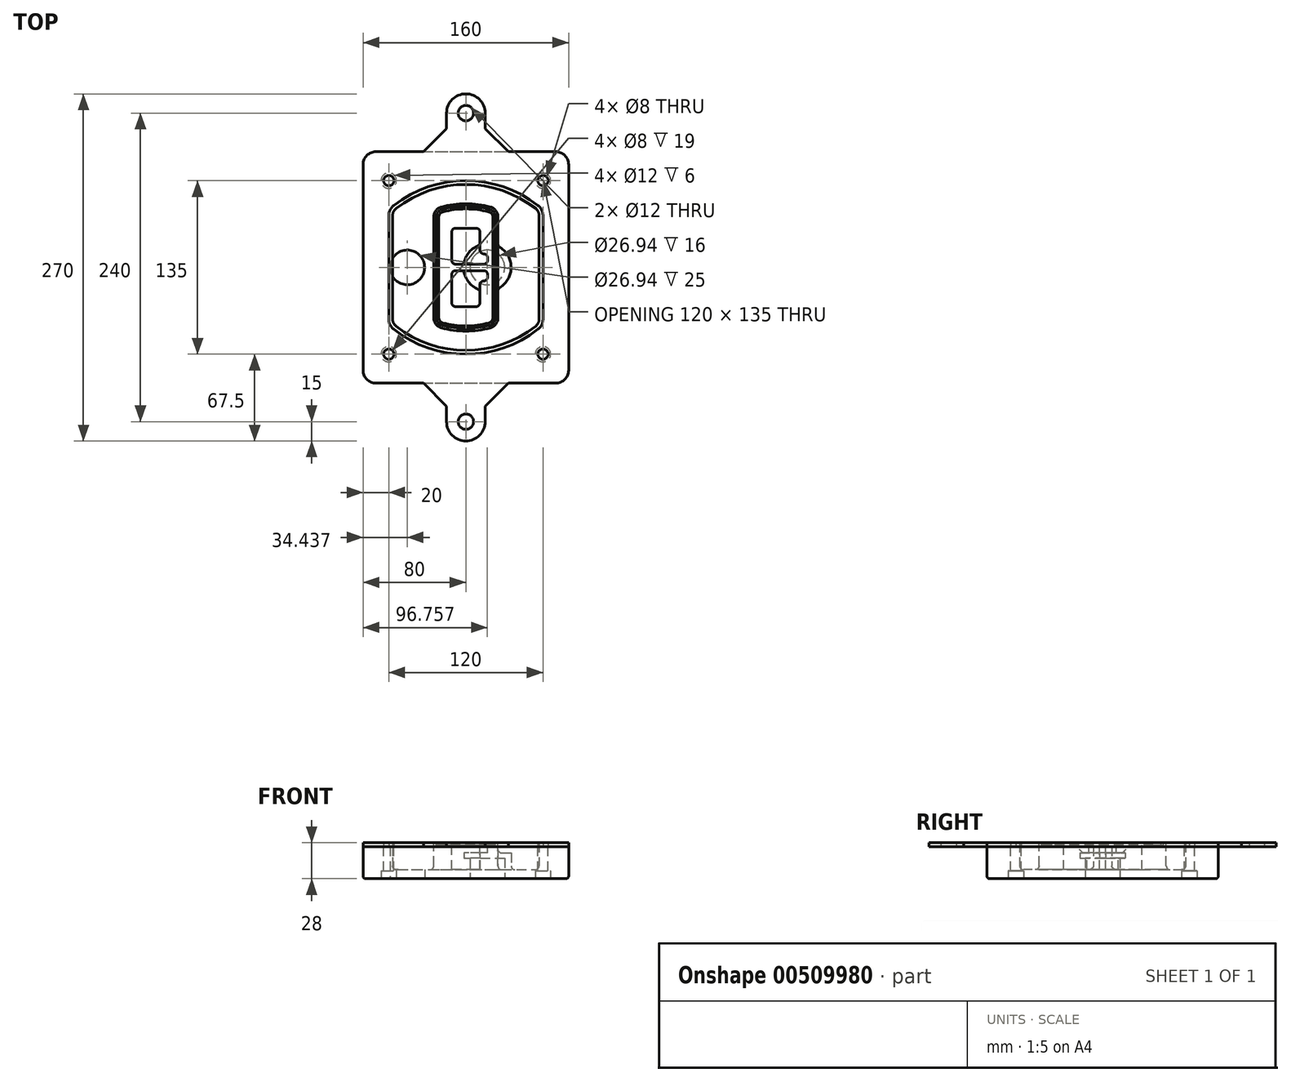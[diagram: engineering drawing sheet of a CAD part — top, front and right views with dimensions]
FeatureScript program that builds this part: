
annotation { "Feature Type Name" : "Feature", "Feature Type Description" : "" }
export const myFeature = defineFeature(function(context is Context, id is Id, definition is map)
    precondition{}
    {
        {
            var Q0;
            Q0=qCreatedBy(makeId("Top.planeOp"),FACE);
            var sketch = newSketch(context, id + "F0", { "sketchPlane" : qUnion([Q0])});
            skPoint(sketch, "E0.rect.middle", {"position": v(0, 0) * mm});
            skLineSegment(sketch, "E1.bottom", {"start": v(-70, -90) * mm, "end": v(70, -90) * mm});
            skLineSegment(sketch, "E1.top", {"start": v(-70, 90) * mm, "end": v(70, 90) * mm});
            skLineSegment(sketch, "E1.left", {"start": v(-80, -80) * mm, "end": v(-80, 80) * mm});
            skLineSegment(sketch, "E1.right", {"start": v(80, -80) * mm, "end": v(80, 80) * mm});
            skLineSegment(sketch, "E2", {"start": v(-80, 90) * mm, "end": v(80, -90) * mm, "construction": true});
            skLineSegment(sketch, "E3", {"start": v(80, 90) * mm, "end": v(-80, -90) * mm, "construction": true});
            skCircle(sketch, "E4", {"center": v(-60, 67.5) * mm, "radius": 4 * mm});
            skCircle(sketch, "E5", {"center": v(60, 67.5) * mm, "radius": 4 * mm});
            skCircle(sketch, "E6", {"center": v(60, -67.5) * mm, "radius": 4 * mm});
            skCircle(sketch, "E7", {"center": v(-60, -67.5) * mm, "radius": 4 * mm});
            skLineSegment(sketch, "E8", {"start": v(-60, 67.5) * mm, "end": v(60, 67.5) * mm, "construction": true});
            skLineSegment(sketch, "E9", {"start": v(60, 67.5) * mm, "end": v(60, -67.5) * mm, "construction": true});
            skLineSegment(sketch, "E10", {"start": v(60, -67.5) * mm, "end": v(-60, -67.5) * mm, "construction": true});
            skLineSegment(sketch, "E11", {"start": v(-60, -67.5) * mm, "end": v(-60, 67.5) * mm, "construction": true});
            skLineSegment(sketch, "E12", {"start": v(-60, 40.3) * mm, "end": v(-60, -40.3) * mm});
            skLineSegment(sketch, "E13", {"start": v(60, 40.3) * mm, "end": v(60, -40.3) * mm});
            skArc(sketch, "E14", {"start": v(56.15, 48.18) * mm, "mid": v(0, 67.5) * mm, "end": v(-56.15, 48.18) * mm});
            skArc(sketch, "E15", {"start": v(-56.15, -48.18) * mm, "mid": v(0, -67.5) * mm, "end": v(56.15, -48.18) * mm});
            skLineSegment(sketch, "E16", {"start": v(-60, 0) * mm, "end": v(60, 0) * mm, "construction": true});
            skPoint(sketch, "E17.visualSharp", {"position": v(-60, -45) * mm});
            skArc(sketch, "E17.filletArc", {"start": v(-60, -40.3) * mm, "mid": v(-58.99, -44.68) * mm, "end": v(-56.15, -48.18) * mm});
            skPoint(sketch, "E18.visualSharp", {"position": v(-60, 45) * mm});
            skArc(sketch, "E18.filletArc", {"start": v(-56.15, 48.18) * mm, "mid": v(-58.99, 44.68) * mm, "end": v(-60, 40.3) * mm});
            skPoint(sketch, "E19.visualSharp", {"position": v(60, 45) * mm});
            skArc(sketch, "E19.filletArc", {"start": v(60, 40.3) * mm, "mid": v(58.99, 44.68) * mm, "end": v(56.15, 48.18) * mm});
            skPoint(sketch, "E20.visualSharp", {"position": v(60, -45) * mm});
            skArc(sketch, "E20.filletArc", {"start": v(56.15, -48.18) * mm, "mid": v(58.99, -44.68) * mm, "end": v(60, -40.3) * mm});
            skPoint(sketch, "E21.visualSharp", {"position": v(-80, 90) * mm});
            skArc(sketch, "E21.filletArc", {"start": v(-70, 90) * mm, "mid": v(-77.07, 87.07) * mm, "end": v(-80, 80) * mm});
            skPoint(sketch, "E22.visualSharp", {"position": v(80, 90) * mm});
            skArc(sketch, "E22.filletArc", {"start": v(80, 80) * mm, "mid": v(77.07, 87.07) * mm, "end": v(70, 90) * mm});
            skPoint(sketch, "E23.visualSharp", {"position": v(80, -90) * mm});
            skArc(sketch, "E23.filletArc", {"start": v(70, -90) * mm, "mid": v(77.07, -87.07) * mm, "end": v(80, -80) * mm});
            skPoint(sketch, "E24.visualSharp", {"position": v(-80, -90) * mm});
            skArc(sketch, "E24.filletArc", {"start": v(-80, -80) * mm, "mid": v(-77.07, -87.07) * mm, "end": v(-70, -90) * mm});
            skArc(sketch, "E25.0", {"start": v(57, 40.3) * mm, "mid": v(56.3, 43.36) * mm, "end": v(54.3, 45.81) * mm});
            skLineSegment(sketch, "E25.1", {"start": v(57, 40.3) * mm, "end": v(57, -40.3) * mm});
            skArc(sketch, "E25.2", {"start": v(54.3, -45.81) * mm, "mid": v(56.3, -43.36) * mm, "end": v(57, -40.3) * mm});
            skArc(sketch, "E25.3", {"start": v(-54.3, -45.81) * mm, "mid": v(0, -64.5) * mm, "end": v(54.3, -45.81) * mm});
            skArc(sketch, "E25.4", {"start": v(-57, -40.3) * mm, "mid": v(-56.3, -43.36) * mm, "end": v(-54.3, -45.81) * mm});
            skArc(sketch, "E25.5", {"start": v(54.3, 45.81) * mm, "mid": v(0, 64.5) * mm, "end": v(-54.3, 45.81) * mm});
            skLineSegment(sketch, "E25.6", {"start": v(-57, 40.3) * mm, "end": v(-57, -40.3) * mm});
            skArc(sketch, "E25.7", {"start": v(-54.3, 45.81) * mm, "mid": v(-56.3, 43.36) * mm, "end": v(-57, 40.3) * mm});
            skArc(sketch, "E26.0", {"start": v(-58.62, 51.33) * mm, "mid": v(-62.58, 46.43) * mm, "end": v(-64, 40.3) * mm});
            skArc(sketch, "E26.1", {"start": v(58.62, 51.33) * mm, "mid": v(0, 71.5) * mm, "end": v(-58.62, 51.33) * mm});
            skArc(sketch, "E26.2", {"start": v(64, 40.3) * mm, "mid": v(62.58, 46.43) * mm, "end": v(58.62, 51.33) * mm});
            skLineSegment(sketch, "E26.3", {"start": v(64, 40.3) * mm, "end": v(64, -40.3) * mm});
            skArc(sketch, "E26.4", {"start": v(58.62, -51.33) * mm, "mid": v(62.58, -46.43) * mm, "end": v(64, -40.3) * mm});
            skLineSegment(sketch, "E26.5", {"start": v(-64, 40.3) * mm, "end": v(-64, -40.3) * mm});
            skArc(sketch, "E26.6", {"start": v(-58.62, -51.33) * mm, "mid": v(0, -71.5) * mm, "end": v(58.62, -51.33) * mm});
            skArc(sketch, "E26.7", {"start": v(-64, -40.3) * mm, "mid": v(-62.58, -46.43) * mm, "end": v(-58.62, -51.33) * mm});
            skSolve(sketch);
        }
        {
            var Q0;
            Q0=makeQuery(id+"F0.imprint","IMPRINT",FACE,{"disambiguationData":[TD([[makeQuery(id+"F0.imprint","IMPRINT",EDGE,{"derivedFrom":sQuery(id+"F0.wireOp",EDGE,"E1.bottom")}),1.0]])]});
            var Q1;
            Q1=makeQuery(id+"F0.imprint","IMPRINT",FACE,{"disambiguationData":[TD([[makeQuery(id+"F0.imprint","IMPRINT",EDGE,{"derivedFrom":sQuery(id+"F0.wireOp",EDGE,"E12")}),1.0]])]});
            var Q2;
            Q2=makeQuery(id+"F0.imprint","IMPRINT",FACE,{"disambiguationData":[TD([[makeQuery(id+"F0.imprint","IMPRINT",EDGE,{"derivedFrom":sQuery(id+"F0.wireOp",EDGE,"E25.0")}),1.0]])]});
            var Q3;
            Q3=makeQuery(id+"F0.imprint","IMPRINT",FACE,{"disambiguationData":[TD([[makeQuery(id+"F0.imprint","IMPRINT",EDGE,{"derivedFrom":sQuery(id+"F0.wireOp",EDGE,"E12")}),-1.0]])]});
            extrude(context, id + "F1", {"entities" : qUnion([Q0, Q1, Q2, Q3]), "oppositeDirection" : true, "depth" : 25 * mm});
        }
        {
            var Q0;
            Q0=makeQuery(id+"F0.imprint","IMPRINT",FACE,{"disambiguationData":[TD([[makeQuery(id+"F0.imprint","IMPRINT",EDGE,{"derivedFrom":sQuery(id+"F0.wireOp",EDGE,"E12")}),1.0]])]});
            extrude(context, id + "F2", {"entities" : qUnion([Q0]), "operationType" : NewBodyOperationType.ADD, "depth" : 3 * mm});
        }
        {
            var Q0;
            Q0=makeQuery(id+"F0.imprint","IMPRINT",FACE,{"disambiguationData":[TD([[makeQuery(id+"F0.imprint","IMPRINT",EDGE,{"derivedFrom":sQuery(id+"F0.wireOp",EDGE,"E25.0")}),1.0]])]});
            extrude(context, id + "F3", {"entities" : qUnion([Q0]), "operationType" : NewBodyOperationType.REMOVE, "oppositeDirection" : true, "depth" : 18 * mm});
        }
        {
            var Q0;
            Q0=makeQuery(id+"F2.opExtrude","CAP_FACE",FACE,{"disambiguationData":[OSD([sQuery(id+"F0.wireOp",EDGE,"E12"),sQuery(id+"F0.wireOp",EDGE,"E13"),sQuery(id+"F0.wireOp",EDGE,"E14"),sQuery(id+"F0.wireOp",EDGE,"E15"),sQuery(id+"F0.wireOp",EDGE,"E17.filletArc"),sQuery(id+"F0.wireOp",EDGE,"E18.filletArc"),sQuery(id+"F0.wireOp",EDGE,"E19.filletArc"),sQuery(id+"F0.wireOp",EDGE,"E20.filletArc"),sQuery(id+"F0.wireOp",EDGE,"E25.0"),sQuery(id+"F0.wireOp",EDGE,"E25.1"),sQuery(id+"F0.wireOp",EDGE,"E25.2"),sQuery(id+"F0.wireOp",EDGE,"E25.3"),sQuery(id+"F0.wireOp",EDGE,"E25.4"),sQuery(id+"F0.wireOp",EDGE,"E25.5"),sQuery(id+"F0.wireOp",EDGE,"E25.6"),sQuery(id+"F0.wireOp",EDGE,"E25.7")])],"isStart":false});
            var sketch = newSketch(context, id + "F4", { "sketchPlane" : qUnion([Q0])});
            skArc(sketch, "E27.0", {"start": v(-19.08, -46.97) * mm, "mid": v(0, -49.5) * mm, "end": v(19.08, -46.97) * mm});
            skArc(sketch, "E28.0", {"start": v(19.08, 46.97) * mm, "mid": v(0, 49.5) * mm, "end": v(-19.08, 46.97) * mm});
            skLineSegment(sketch, "E29", {"start": v(-25, 39.25) * mm, "end": v(-25, -39.25) * mm});
            skLineSegment(sketch, "E30", {"start": v(25, 39.25) * mm, "end": v(25, -39.25) * mm});
            skLineSegment(sketch, "E31", {"start": v(-25, 45.1) * mm, "end": v(25, 45.1) * mm, "construction": true});
            skLineSegment(sketch, "E32", {"start": v(-25, -45.1) * mm, "end": v(25, -45.1) * mm, "construction": true});
            skPoint(sketch, "E33.visualSharp", {"position": v(-25, 45.1) * mm});
            skArc(sketch, "E33.filletArc", {"start": v(-19.08, 46.97) * mm, "mid": v(-23.35, 44.11) * mm, "end": v(-25, 39.25) * mm});
            skPoint(sketch, "E34.visualSharp", {"position": v(25, 45.1) * mm});
            skArc(sketch, "E34.filletArc", {"start": v(25, 39.25) * mm, "mid": v(23.35, 44.11) * mm, "end": v(19.08, 46.97) * mm});
            skPoint(sketch, "E35.visualSharp", {"position": v(25, -45.1) * mm});
            skArc(sketch, "E35.filletArc", {"start": v(19.08, -46.97) * mm, "mid": v(23.35, -44.11) * mm, "end": v(25, -39.25) * mm});
            skPoint(sketch, "E36.visualSharp", {"position": v(-25, -45.1) * mm});
            skArc(sketch, "E36.filletArc", {"start": v(-25, -39.25) * mm, "mid": v(-23.35, -44.11) * mm, "end": v(-19.08, -46.97) * mm});
            skArc(sketch, "E37.0", {"start": v(54.3, 45.81) * mm, "mid": v(0, 64.5) * mm, "end": v(-54.3, 45.81) * mm});
            skArc(sketch, "E37.1", {"start": v(-54.3, 45.81) * mm, "mid": v(-56.3, 43.36) * mm, "end": v(-57, 40.3) * mm});
            skLineSegment(sketch, "E37.2", {"start": v(-57, 40.3) * mm, "end": v(-57, -40.3) * mm});
            skArc(sketch, "E37.3", {"start": v(-57, -40.3) * mm, "mid": v(-56.3, -43.36) * mm, "end": v(-54.3, -45.81) * mm});
            skArc(sketch, "E37.4", {"start": v(-54.3, -45.81) * mm, "mid": v(0, -64.5) * mm, "end": v(54.3, -45.81) * mm});
            skArc(sketch, "E37.5", {"start": v(54.3, -45.81) * mm, "mid": v(56.3, -43.36) * mm, "end": v(57, -40.3) * mm});
            skLineSegment(sketch, "E37.6", {"start": v(57, 40.3) * mm, "end": v(57, -40.3) * mm});
            skArc(sketch, "E37.7", {"start": v(57, 40.3) * mm, "mid": v(56.3, 43.36) * mm, "end": v(54.3, 45.81) * mm});
            skLineSegment(sketch, "E38.0", {"start": v(23, 39.25) * mm, "end": v(23, -39.25) * mm});
            skArc(sketch, "E38.1", {"start": v(18.56, -45.04) * mm, "mid": v(21.76, -42.9) * mm, "end": v(23, -39.25) * mm});
            skArc(sketch, "E38.2", {"start": v(-18.56, -45.04) * mm, "mid": v(0, -47.5) * mm, "end": v(18.56, -45.04) * mm});
            skArc(sketch, "E38.3", {"start": v(-23, -39.25) * mm, "mid": v(-21.76, -42.9) * mm, "end": v(-18.56, -45.04) * mm});
            skLineSegment(sketch, "E38.4", {"start": v(-23, 39.25) * mm, "end": v(-23, -39.25) * mm});
            skArc(sketch, "E38.5", {"start": v(23, 39.25) * mm, "mid": v(21.76, 42.9) * mm, "end": v(18.56, 45.04) * mm});
            skArc(sketch, "E38.6", {"start": v(-18.56, 45.04) * mm, "mid": v(-21.76, 42.9) * mm, "end": v(-23, 39.25) * mm});
            skArc(sketch, "E38.7", {"start": v(18.56, 45.04) * mm, "mid": v(0, 47.5) * mm, "end": v(-18.56, 45.04) * mm});
            skArc(sketch, "E39.0", {"start": v(21, 39.25) * mm, "mid": v(20.18, 41.68) * mm, "end": v(18.04, 43.1) * mm});
            skLineSegment(sketch, "E39.1", {"start": v(21, 39.25) * mm, "end": v(21, -39.25) * mm});
            skArc(sketch, "E39.2", {"start": v(18.04, -43.1) * mm, "mid": v(20.18, -41.68) * mm, "end": v(21, -39.25) * mm});
            skArc(sketch, "E39.3", {"start": v(-18.04, -43.1) * mm, "mid": v(0, -45.5) * mm, "end": v(18.04, -43.1) * mm});
            skArc(sketch, "E39.4", {"start": v(-21, -39.25) * mm, "mid": v(-20.18, -41.68) * mm, "end": v(-18.04, -43.1) * mm});
            skArc(sketch, "E39.5", {"start": v(18.04, 43.1) * mm, "mid": v(0, 45.5) * mm, "end": v(-18.04, 43.1) * mm});
            skLineSegment(sketch, "E39.6", {"start": v(-21, 39.25) * mm, "end": v(-21, -39.25) * mm});
            skArc(sketch, "E39.7", {"start": v(-18.04, 43.1) * mm, "mid": v(-20.18, 41.68) * mm, "end": v(-21, 39.25) * mm});
            skLineSegment(sketch, "E40", {"start": v(-25, 0) * mm, "end": v(25, 0) * mm, "construction": true});
            skLineSegment(sketch, "E41", {"start": v(-11, 5.5) * mm, "end": v(-11, 27.5) * mm});
            skLineSegment(sketch, "E42", {"start": v(-8, 30.5) * mm, "end": v(8, 30.5) * mm});
            skLineSegment(sketch, "E43", {"start": v(11, 27.5) * mm, "end": v(11, 13.5) * mm});
            skLineSegment(sketch, "E44", {"start": v(14, 10.5) * mm, "end": v(14, 10.5) * mm});
            skLineSegment(sketch, "E45", {"start": v(17, 7.5) * mm, "end": v(17, 5.5) * mm});
            skLineSegment(sketch, "E46", {"start": v(14, 2.5) * mm, "end": v(-8, 2.5) * mm});
            skPoint(sketch, "E47.visualSharp", {"position": v(-11, 30.5) * mm});
            skArc(sketch, "E47.filletArc", {"start": v(-8, 30.5) * mm, "mid": v(-10.12, 29.62) * mm, "end": v(-11, 27.5) * mm});
            skPoint(sketch, "E48.visualSharp", {"position": v(11, 30.5) * mm});
            skArc(sketch, "E48.filletArc", {"start": v(11, 27.5) * mm, "mid": v(10.12, 29.62) * mm, "end": v(8, 30.5) * mm});
            skPoint(sketch, "E49.visualSharp", {"position": v(11, 10.5) * mm});
            skArc(sketch, "E49.filletArc", {"start": v(11, 13.5) * mm, "mid": v(11.88, 11.38) * mm, "end": v(14, 10.5) * mm});
            skPoint(sketch, "E50.visualSharp", {"position": v(17, 10.5) * mm});
            skArc(sketch, "E50.filletArc", {"start": v(17, 7.5) * mm, "mid": v(16.12, 9.62) * mm, "end": v(14, 10.5) * mm});
            skPoint(sketch, "E51.visualSharp", {"position": v(17, 2.5) * mm});
            skArc(sketch, "E51.filletArc", {"start": v(14, 2.5) * mm, "mid": v(16.12, 3.38) * mm, "end": v(17, 5.5) * mm});
            skPoint(sketch, "E52.visualSharp", {"position": v(-11, 2.5) * mm});
            skArc(sketch, "E52.filletArc", {"start": v(-11, 5.5) * mm, "mid": v(-10.12, 3.38) * mm, "end": v(-8, 2.5) * mm});
            skLineSegment(sketch, "E53.0.MirrorCS", {"start": v(14, -2.5) * mm, "end": v(-8, -2.5) * mm});
            skArc(sketch, "E54.0.MirrorCS", {"start": v(-11, -5.5) * mm, "mid": v(-10.12, -3.38) * mm, "end": v(-8, -2.5) * mm});
            skLineSegment(sketch, "E55.0.MirrorCS", {"start": v(-11, -5.5) * mm, "end": v(-11, -27.5) * mm});
            skArc(sketch, "E56.0.MirrorCS", {"start": v(-8, -30.5) * mm, "mid": v(-10.12, -29.62) * mm, "end": v(-11, -27.5) * mm});
            skLineSegment(sketch, "E57.0.MirrorCS", {"start": v(-8, -30.5) * mm, "end": v(8, -30.5) * mm});
            skArc(sketch, "E58.0.MirrorCS", {"start": v(11, -27.5) * mm, "mid": v(10.12, -29.62) * mm, "end": v(8, -30.5) * mm});
            skLineSegment(sketch, "E59.0.MirrorCS", {"start": v(11, -27.5) * mm, "end": v(11, -13.5) * mm});
            skArc(sketch, "E60.0.MirrorCS", {"start": v(11, -13.5) * mm, "mid": v(11.88, -11.38) * mm, "end": v(14, -10.5) * mm});
            skArc(sketch, "E61.0.MirrorCS", {"start": v(17, -7.5) * mm, "mid": v(16.12, -9.62) * mm, "end": v(14, -10.5) * mm});
            skLineSegment(sketch, "E62.0.MirrorCS", {"start": v(17, -7.5) * mm, "end": v(17, -5.5) * mm});
            skArc(sketch, "E63.0.MirrorCS", {"start": v(14, -2.5) * mm, "mid": v(16.12, -3.38) * mm, "end": v(17, -5.5) * mm});
            skSolve(sketch);
        }
        {
            var Q0;
            Q0=makeQuery(id+"F4.imprint","IMPRINT",FACE,{"disambiguationData":[TD([[makeQuery(id+"F4.imprint","IMPRINT",EDGE,{"derivedFrom":sQuery(id+"F4.wireOp",EDGE,"E27.0")}),1.0]])]});
            var Q1;
            Q1=makeQuery(id+"F4.imprint","IMPRINT",FACE,{"disambiguationData":[TD([[makeQuery(id+"F4.imprint","IMPRINT",EDGE,{"derivedFrom":sQuery(id+"F4.wireOp",EDGE,"E38.0")}),-1.0]])]});
            var Q2;
            Q2=makeQuery(id+"F4.imprint","IMPRINT",FACE,{"disambiguationData":[TD([[makeQuery(id+"F4.imprint","IMPRINT",EDGE,{"derivedFrom":sQuery(id+"F4.wireOp",EDGE,"E39.0")}),1.0]])]});
            extrude(context, id + "F5", {"entities" : qUnion([Q0, Q1, Q2]), "operationType" : NewBodyOperationType.ADD, "endBound" : BoundingType.UP_TO_NEXT, "oppositeDirection" : true, "depth" : 25 * mm});
        }
        {
            var Q0;
            Q0=makeQuery(id+"F4.imprint","IMPRINT",FACE,{"disambiguationData":[TD([[makeQuery(id+"F4.imprint","IMPRINT",EDGE,{"derivedFrom":sQuery(id+"F4.wireOp",EDGE,"E38.0")}),-1.0]])]});
            extrude(context, id + "F6", {"entities" : qUnion([Q0]), "operationType" : NewBodyOperationType.REMOVE, "oppositeDirection" : true, "depth" : 2 * mm});
        }
        {
            var Q0;
            Q0=makeQuery(id+"F1.opExtrude","CAP_FACE",FACE,{"disambiguationData":[OSD([sQuery(id+"F0.wireOp",EDGE,"E1.bottom"),sQuery(id+"F0.wireOp",EDGE,"E1.top"),sQuery(id+"F0.wireOp",EDGE,"E1.left"),sQuery(id+"F0.wireOp",EDGE,"E1.right"),sQuery(id+"F0.wireOp",EDGE,"E4"),sQuery(id+"F0.wireOp",EDGE,"E5"),sQuery(id+"F0.wireOp",EDGE,"E6"),sQuery(id+"F0.wireOp",EDGE,"E7"),sQuery(id+"F0.wireOp",EDGE,"E21.filletArc"),sQuery(id+"F0.wireOp",EDGE,"E22.filletArc"),sQuery(id+"F0.wireOp",EDGE,"E23.filletArc"),sQuery(id+"F0.wireOp",EDGE,"E24.filletArc")])],"isStart":false});
            var sketch = newSketch(context, id + "F7", { "sketchPlane" : qUnion([Q0])});
            skCircle(sketch, "E64", {"center": v(16.76, 0) * mm, "radius": 13.47 * mm});
            skCircle(sketch, "E65", {"center": v(-45.56, 0) * mm, "radius": 13.47 * mm});
            skLineSegment(sketch, "E66", {"start": v(80, 0) * mm, "end": v(-80, 0) * mm});
            skCircle(sketch, "E67", {"center": v(16.76, 0) * mm, "radius": 18.47 * mm});
            skCircle(sketch, "E68", {"center": v(60, -67.5) * mm, "radius": 6 * mm});
            skCircle(sketch, "E69", {"center": v(-60, -67.5) * mm, "radius": 6 * mm});
            skCircle(sketch, "E70", {"center": v(-60, 67.5) * mm, "radius": 6 * mm});
            skCircle(sketch, "E71", {"center": v(60, 67.5) * mm, "radius": 6 * mm});
            skSolve(sketch);
        }
        {
            var Q0;
            {var subQ1=sQuery(id+"F7.wireOp",EDGE,"E66");var subQ4=sQuery(id+"F7.wireOp",EDGE,"E64");var subQ6=makeQuery(id+"F7.imprint","INTERSECT",VERTEX,{"disambiguationData":[OD(0.0)],"derivedFrom":[subQ4,subQ1]});Q0=makeQuery(id+"F7.imprint","IMPRINT",FACE,{"disambiguationData":[TD([[makeQuery(id+"F7.imprint","IMPRINT",EDGE,{"disambiguationData":[TD([[subQ6,-1.0]])],"derivedFrom":subQ4}),-1.0]])]});}
            var Q1;
            {var subQ0=sQuery(id+"F7.wireOp",EDGE,"E66");var subQ1=sQuery(id+"F7.wireOp",EDGE,"E64");var subQ3=makeQuery(id+"F7.imprint","INTERSECT",VERTEX,{"disambiguationData":[OD(0.0)],"derivedFrom":[subQ1,subQ0]});Q1=makeQuery(id+"F7.imprint","IMPRINT",FACE,{"disambiguationData":[TD([[makeQuery(id+"F7.imprint","IMPRINT",EDGE,{"disambiguationData":[TD([[subQ3,-1.0]])],"derivedFrom":subQ1}),1.0]])]});}
            var Q2;
            {var subQ0=sQuery(id+"F7.wireOp",EDGE,"E66");var subQ1=sQuery(id+"F7.wireOp",EDGE,"E64");var subQ3=makeQuery(id+"F7.imprint","INTERSECT",VERTEX,{"disambiguationData":[OD(0.0)],"derivedFrom":[subQ1,subQ0]});Q2=makeQuery(id+"F7.imprint","IMPRINT",FACE,{"disambiguationData":[TD([[makeQuery(id+"F7.imprint","IMPRINT",EDGE,{"disambiguationData":[TD([[subQ3,1.0]])],"derivedFrom":subQ1}),1.0]])]});}
            var Q3;
            {var subQ1=sQuery(id+"F7.wireOp",EDGE,"E66");var subQ4=sQuery(id+"F7.wireOp",EDGE,"E64");var subQ6=makeQuery(id+"F7.imprint","INTERSECT",VERTEX,{"disambiguationData":[OD(0.0)],"derivedFrom":[subQ4,subQ1]});Q3=makeQuery(id+"F7.imprint","IMPRINT",FACE,{"disambiguationData":[TD([[makeQuery(id+"F7.imprint","IMPRINT",EDGE,{"disambiguationData":[TD([[subQ6,1.0]])],"derivedFrom":subQ4}),-1.0]])]});}
            extrude(context, id + "F8", {"entities" : qUnion([Q0, Q1, Q2, Q3]), "operationType" : NewBodyOperationType.ADD, "oppositeDirection" : true, "depth" : 20 * mm});
        }
        {
            var Q0;
            {var subQ0=sQuery(id+"F7.wireOp",EDGE,"E66");var subQ1=sQuery(id+"F7.wireOp",EDGE,"E64");var subQ3=makeQuery(id+"F7.imprint","INTERSECT",VERTEX,{"disambiguationData":[OD(0.0)],"derivedFrom":[subQ1,subQ0]});Q0=makeQuery(id+"F7.imprint","IMPRINT",FACE,{"disambiguationData":[TD([[makeQuery(id+"F7.imprint","IMPRINT",EDGE,{"disambiguationData":[TD([[subQ3,-1.0]])],"derivedFrom":subQ1}),1.0]])]});}
            var Q1;
            {var subQ0=sQuery(id+"F7.wireOp",EDGE,"E66");var subQ1=sQuery(id+"F7.wireOp",EDGE,"E64");var subQ3=makeQuery(id+"F7.imprint","INTERSECT",VERTEX,{"disambiguationData":[OD(0.0)],"derivedFrom":[subQ1,subQ0]});Q1=makeQuery(id+"F7.imprint","IMPRINT",FACE,{"disambiguationData":[TD([[makeQuery(id+"F7.imprint","IMPRINT",EDGE,{"disambiguationData":[TD([[subQ3,1.0]])],"derivedFrom":subQ1}),1.0]])]});}
            extrude(context, id + "F9", {"entities" : qUnion([Q0, Q1]), "operationType" : NewBodyOperationType.REMOVE, "oppositeDirection" : true, "depth" : 16 * mm});
        }
        {
            var Q0;
            {var subQ0=sQuery(id+"F7.wireOp",EDGE,"E66");var subQ1=sQuery(id+"F7.wireOp",EDGE,"E65");var subQ3=makeQuery(id+"F7.imprint","INTERSECT",VERTEX,{"disambiguationData":[OD(0.0)],"derivedFrom":[subQ1,subQ0]});Q0=makeQuery(id+"F7.imprint","IMPRINT",FACE,{"disambiguationData":[TD([[makeQuery(id+"F7.imprint","IMPRINT",EDGE,{"disambiguationData":[TD([[subQ3,-1.0]])],"derivedFrom":subQ1}),1.0]])]});}
            var Q1;
            {var subQ0=sQuery(id+"F7.wireOp",EDGE,"E66");var subQ1=sQuery(id+"F7.wireOp",EDGE,"E65");var subQ3=makeQuery(id+"F7.imprint","INTERSECT",VERTEX,{"disambiguationData":[OD(0.0)],"derivedFrom":[subQ1,subQ0]});Q1=makeQuery(id+"F7.imprint","IMPRINT",FACE,{"disambiguationData":[TD([[makeQuery(id+"F7.imprint","IMPRINT",EDGE,{"disambiguationData":[TD([[subQ3,1.0]])],"derivedFrom":subQ1}),1.0]])]});}
            extrude(context, id + "F10", {"entities" : qUnion([Q0, Q1]), "operationType" : NewBodyOperationType.REMOVE, "oppositeDirection" : true, "depth" : 25 * mm});
        }
        {
            var Q0;
            Q0=makeQuery(id+"F7.imprint","IMPRINT",FACE,{"disambiguationData":[TD([[makeQuery(id+"F7.imprint","IMPRINT",EDGE,{"derivedFrom":sQuery(id+"F7.wireOp",EDGE,"E68")}),1.0]])]});
            var Q1;
            Q1=makeQuery(id+"F7.imprint","IMPRINT",FACE,{"disambiguationData":[TD([[makeQuery(id+"F7.imprint","IMPRINT",EDGE,{"derivedFrom":makeQuery(id+"F1.opExtrude","CAP_EDGE",EDGE,{"disambiguationData":[OSD([sQuery(id+"F0.wireOp",EDGE,"E5")])],"isStart":false})}),-1.0]])]});
            var Q2;
            Q2=makeQuery(id+"F7.imprint","IMPRINT",FACE,{"disambiguationData":[TD([[makeQuery(id+"F7.imprint","IMPRINT",EDGE,{"derivedFrom":sQuery(id+"F7.wireOp",EDGE,"E69")}),1.0]])]});
            var Q3;
            Q3=makeQuery(id+"F7.imprint","IMPRINT",FACE,{"disambiguationData":[TD([[makeQuery(id+"F7.imprint","IMPRINT",EDGE,{"derivedFrom":makeQuery(id+"F1.opExtrude","CAP_EDGE",EDGE,{"disambiguationData":[OSD([sQuery(id+"F0.wireOp",EDGE,"E4")])],"isStart":false})}),-1.0]])]});
            var Q4;
            Q4=makeQuery(id+"F7.imprint","IMPRINT",FACE,{"disambiguationData":[TD([[makeQuery(id+"F7.imprint","IMPRINT",EDGE,{"derivedFrom":sQuery(id+"F7.wireOp",EDGE,"E70")}),1.0]])]});
            var Q5;
            Q5=makeQuery(id+"F7.imprint","IMPRINT",FACE,{"disambiguationData":[TD([[makeQuery(id+"F7.imprint","IMPRINT",EDGE,{"derivedFrom":makeQuery(id+"F1.opExtrude","CAP_EDGE",EDGE,{"disambiguationData":[OSD([sQuery(id+"F0.wireOp",EDGE,"E7")])],"isStart":false})}),-1.0]])]});
            var Q6;
            Q6=makeQuery(id+"F7.imprint","IMPRINT",FACE,{"disambiguationData":[TD([[makeQuery(id+"F7.imprint","IMPRINT",EDGE,{"derivedFrom":sQuery(id+"F7.wireOp",EDGE,"E71")}),1.0]])]});
            var Q7;
            Q7=makeQuery(id+"F7.imprint","IMPRINT",FACE,{"disambiguationData":[TD([[makeQuery(id+"F7.imprint","IMPRINT",EDGE,{"derivedFrom":makeQuery(id+"F1.opExtrude","CAP_EDGE",EDGE,{"disambiguationData":[OSD([sQuery(id+"F0.wireOp",EDGE,"E6")])],"isStart":false})}),-1.0]])]});
            extrude(context, id + "F11", {"entities" : qUnion([Q0, Q1, Q2, Q3, Q4, Q5, Q6, Q7]), "operationType" : NewBodyOperationType.REMOVE, "oppositeDirection" : true, "depth" : 6 * mm});
        }
        {
            var Q0;
            Q0=makeQuery(id+"F9.boolean.opBoolean","COPY",FACE,{"derivedFrom":makeQuery(id+"F9.opExtrude","CAP_FACE",FACE,{"disambiguationData":[OSD([sQuery(id+"F7.wireOp",EDGE,"E64")])],"isStart":false})});
            var sketch = newSketch(context, id + "F12", { "sketchPlane" : qUnion([Q0])});
            skArc(sketch, "E72.0", {"start": v(11, 17.55) * mm, "mid": v(2.57, 11.82) * mm, "end": v(-1.54, 2.5) * mm});
            skArc(sketch, "E72.1", {"start": v(-1.54, -2.5) * mm, "mid": v(2.57, -11.82) * mm, "end": v(11, -17.55) * mm});
            skLineSegment(sketch, "E73", {"start": v(-1.54, -2.5) * mm, "end": v(14, -2.5) * mm});
            skLineSegment(sketch, "E74.0", {"start": v(14, 2.5) * mm, "end": v(-1.54, 2.5) * mm});
            skArc(sketch, "E74.1", {"start": v(14, 2.5) * mm, "mid": v(16.12, 3.38) * mm, "end": v(17, 5.5) * mm});
            skLineSegment(sketch, "E74.2", {"start": v(17, 7.5) * mm, "end": v(17, 5.5) * mm});
            skArc(sketch, "E74.3", {"start": v(17, 7.5) * mm, "mid": v(16.12, 9.62) * mm, "end": v(14, 10.5) * mm});
            skArc(sketch, "E74.4", {"start": v(11, 13.5) * mm, "mid": v(11.88, 11.38) * mm, "end": v(14, 10.5) * mm});
            skLineSegment(sketch, "E74.5", {"start": v(11, 17.55) * mm, "end": v(11, 13.5) * mm});
            skLineSegment(sketch, "E74.7", {"start": v(14, -2.5) * mm, "end": v(-1.54, -2.5) * mm});
            skArc(sketch, "E74.8", {"start": v(14, -2.5) * mm, "mid": v(16.12, -3.38) * mm, "end": v(17, -5.5) * mm});
            skLineSegment(sketch, "E74.9", {"start": v(17, -7.5) * mm, "end": v(17, -5.5) * mm});
            skArc(sketch, "E74.10", {"start": v(17, -7.5) * mm, "mid": v(16.12, -9.62) * mm, "end": v(14, -10.5) * mm});
            skArc(sketch, "E74.11", {"start": v(11, -13.5) * mm, "mid": v(11.88, -11.38) * mm, "end": v(14, -10.5) * mm});
            skLineSegment(sketch, "E74.12", {"start": v(11, -17.55) * mm, "end": v(11, -13.5) * mm});
            skPoint(sketch, "E75.orphan", {"position": v(11, -27.5) * mm});
            skPoint(sketch, "E76.orphan", {"position": v(-8, -2.5) * mm});
            skPoint(sketch, "E77.orphan", {"position": v(-8, 2.5) * mm});
            skPoint(sketch, "E78.orphan", {"position": v(11, 27.5) * mm});
            skSolve(sketch);
        }
        {
            var Q0;
            {var subQ7=sQuery(id+"F12.wireOp",EDGE,"E72.0");var subQ14=sQuery(id+"F12.wireOp",EDGE,"E72.1");var subQ16=sQuery(id+"F12.wireOp",EDGE,"E74.1");var subQ18=sQuery(id+"F12.wireOp",EDGE,"E74.8");Q0=qUnion([makeQuery(id+"F12.imprint","IMPRINT",FACE,{"disambiguationData":[TD([[makeQuery(id+"F12.imprint","IMPRINT",EDGE,{"derivedFrom":subQ7}),1.0]])]}),makeQuery(id+"F12.imprint","IMPRINT",FACE,{"disambiguationData":[TD([[makeQuery(id+"F12.imprint","IMPRINT",EDGE,{"derivedFrom":subQ14}),1.0]])]}),makeQuery(id+"F12.imprint","IMPRINT",FACE,{"disambiguationData":[TD([[makeQuery(id+"F12.imprint","IMPRINT",EDGE,{"derivedFrom":subQ16}),1.0]])]}),makeQuery(id+"F12.imprint","IMPRINT",FACE,{"disambiguationData":[TD([[makeQuery(id+"F12.imprint","IMPRINT",EDGE,{"derivedFrom":subQ18}),-1.0]])]})]);}
            var Q1;
            Q1=makeQuery(id+"F5.boolean.opBoolean","SPLIT",FACE,{"disambiguationData":[TD([makeQuery(id+"F5.opExtrude","SWEPT_FACE",FACE,{"disambiguationData":[OSD([sQuery(id+"F4.wireOp",EDGE,"E41")])]})])],"derivedFrom":makeQuery(id+"F3.boolean.opBoolean","COPY",FACE,{"derivedFrom":makeQuery(id+"F3.opExtrude","CAP_FACE",FACE,{"disambiguationData":[OSD([sQuery(id+"F0.wireOp",EDGE,"E25.0"),sQuery(id+"F0.wireOp",EDGE,"E25.1"),sQuery(id+"F0.wireOp",EDGE,"E25.2"),sQuery(id+"F0.wireOp",EDGE,"E25.3"),sQuery(id+"F0.wireOp",EDGE,"E25.4"),sQuery(id+"F0.wireOp",EDGE,"E25.5"),sQuery(id+"F0.wireOp",EDGE,"E25.6"),sQuery(id+"F0.wireOp",EDGE,"E25.7")])],"isStart":false})})});
            extrude(context, id + "F13", {"entities" : qUnion([Q0]), "operationType" : NewBodyOperationType.REMOVE, "endBound" : BoundingType.UP_TO_SURFACE, "endBoundEntityFace" : qUnion([Q1]), "depth" : 25 * mm});
        }
        {
            var Q0;
            Q0=makeQuery(id+"F3.boolean.opBoolean","COPY",EDGE,{"derivedFrom":makeQuery(id+"F3.opExtrude","CAP_EDGE",EDGE,{"disambiguationData":[OSD([sQuery(id+"F0.wireOp",EDGE,"E25.6")])],"isStart":false})});
            var Q1;
            Q1=makeQuery(id+"F8.boolean.opBoolean","INTERSECT",EDGE,{"derivedFrom":[makeQuery(id+"F5.opExtrude","SWEPT_FACE",FACE,{"disambiguationData":[OSD([sQuery(id+"F4.wireOp",EDGE,"E30")])]}),makeQuery(id+"F8.opExtrude","CAP_FACE",FACE,{"disambiguationData":[OSD([sQuery(id+"F7.wireOp",EDGE,"E67")])],"isStart":false})]});
            var Q2;
            Q2=makeQuery(id+"F8.boolean.opBoolean","INTERSECT",EDGE,{"disambiguationData":[OD(1.0)],"derivedFrom":[makeQuery(id+"F5.opExtrude","SWEPT_FACE",FACE,{"disambiguationData":[OSD([sQuery(id+"F4.wireOp",EDGE,"E30")])]}),makeQuery(id+"F8.opExtrude","SWEPT_FACE",FACE,{"disambiguationData":[OSD([sQuery(id+"F7.wireOp",EDGE,"E67")])]})]});
            var Q3;
            {var subQ0=sQuery(id+"F4.wireOp",EDGE,"E30");Q3=makeQuery(id+"F8.boolean.opBoolean","SPLIT",EDGE,{"disambiguationData":[TD([makeQuery(id+"F5.opExtrude","SWEPT_FACE",FACE,{"disambiguationData":[OSD([sQuery(id+"F4.wireOp",EDGE,"E35.filletArc")])]})])],"derivedFrom":makeQuery(id+"F5.opExtrude","CAP_EDGE",EDGE,{"disambiguationData":[OSD([subQ0])],"isStart":false})});}
            var Q4;
            {var subQ0=sQuery(id+"F0.wireOp",EDGE,"E25.7");var subQ1=sQuery(id+"F0.wireOp",EDGE,"E25.1");var subQ2=sQuery(id+"F0.wireOp",EDGE,"E25.6");var subQ3=sQuery(id+"F0.wireOp",EDGE,"E25.5");var subQ4=sQuery(id+"F0.wireOp",EDGE,"E25.4");var subQ5=sQuery(id+"F0.wireOp",EDGE,"E25.0");var subQ6=sQuery(id+"F0.wireOp",EDGE,"E25.2");var subQ7=sQuery(id+"F0.wireOp",EDGE,"E25.3");Q4=makeQuery(id+"F8.boolean.opBoolean","INTERSECT",EDGE,{"derivedFrom":[makeQuery(id+"F5.boolean.opBoolean","SPLIT",FACE,{"disambiguationData":[TD([makeQuery(id+"F2.opExtrude","SWEPT_FACE",FACE,{"disambiguationData":[OSD([subQ5])]})])],"derivedFrom":makeQuery(id+"F3.boolean.opBoolean","COPY",FACE,{"derivedFrom":makeQuery(id+"F3.opExtrude","CAP_FACE",FACE,{"disambiguationData":[OSD([subQ5,subQ1,subQ6,subQ7,subQ4,subQ3,subQ2,subQ0])],"isStart":false})})}),makeQuery(id+"F8.opExtrude","SWEPT_FACE",FACE,{"disambiguationData":[OSD([sQuery(id+"F7.wireOp",EDGE,"E67")])]})]});}
            var Q5;
            Q5=makeQuery(id+"F8.boolean.opBoolean","INTERSECT",EDGE,{"disambiguationData":[OD(0.0)],"derivedFrom":[makeQuery(id+"F5.opExtrude","SWEPT_FACE",FACE,{"disambiguationData":[OSD([sQuery(id+"F4.wireOp",EDGE,"E30")])]}),makeQuery(id+"F8.opExtrude","SWEPT_FACE",FACE,{"disambiguationData":[OSD([sQuery(id+"F7.wireOp",EDGE,"E67")])]})]});
            fillet(context, id + "F14", {"entities" : qUnion([Q0, Q1, Q2, Q3, Q4, Q5]), "radius" : 3 * mm, "tangentPropagation" : true, "allowEdgeOverflow" : false});
        }
        {
            var Q0;
            Q0=makeQuery(id+"F1.opExtrude","CAP_EDGE",EDGE,{"disambiguationData":[OSD([sQuery(id+"F0.wireOp",EDGE,"E1.bottom")])],"isStart":false});
            fillet(context, id + "F15", {"entities" : qUnion([Q0]), "radius" : 2 * mm, "tangentPropagation" : true, "allowEdgeOverflow" : false});
        }
        {
            var Q0;
            {var subQ0=sQuery(id+"F0.wireOp",EDGE,"E21.filletArc");var subQ1=sQuery(id+"F0.wireOp",EDGE,"E7");var subQ2=sQuery(id+"F0.wireOp",EDGE,"E6");var subQ3=sQuery(id+"F0.wireOp",EDGE,"E5");var subQ4=sQuery(id+"F0.wireOp",EDGE,"E4");var subQ5=sQuery(id+"F0.wireOp",EDGE,"E22.filletArc");var subQ6=sQuery(id+"F0.wireOp",EDGE,"E1.bottom");var subQ7=sQuery(id+"F0.wireOp",EDGE,"E1.right");var subQ8=sQuery(id+"F0.wireOp",EDGE,"E1.top");var subQ9=sQuery(id+"F0.wireOp",EDGE,"E1.left");var subQ10=sQuery(id+"F0.wireOp",EDGE,"E23.filletArc");var subQ11=sQuery(id+"F0.wireOp",EDGE,"E24.filletArc");Q0=makeQuery(id+"F2.boolean.opBoolean","SPLIT",FACE,{"disambiguationData":[TD([makeQuery(id+"F1.opExtrude","SWEPT_FACE",FACE,{"disambiguationData":[OSD([subQ6])]})])],"derivedFrom":makeQuery(id+"F1.opExtrude","CAP_FACE",FACE,{"disambiguationData":[OSD([subQ6,subQ8,subQ9,subQ7,subQ4,subQ3,subQ2,subQ1,subQ0,subQ5,subQ10,subQ11])],"isStart":true})});}
            var sketch = newSketch(context, id + "F16", { "sketchPlane" : qUnion([Q0])});
            skLineSegment(sketch, "E79.0", {"start": v(-70, -90) * mm, "end": v(70, -90) * mm});
            skArc(sketch, "E79.1", {"start": v(-80, -80) * mm, "mid": v(-77.07, -87.07) * mm, "end": v(-70, -90) * mm});
            skLineSegment(sketch, "E79.2", {"start": v(-80, -80) * mm, "end": v(-80, 80) * mm});
            skLineSegment(sketch, "E79.3", {"start": v(80, -80) * mm, "end": v(80, 80) * mm});
            skArc(sketch, "E79.4", {"start": v(70, -90) * mm, "mid": v(77.07, -87.07) * mm, "end": v(80, -80) * mm});
            skArc(sketch, "E79.5", {"start": v(-70, 90) * mm, "mid": v(-77.07, 87.07) * mm, "end": v(-80, 80) * mm});
            skLineSegment(sketch, "E79.6", {"start": v(-70, 90) * mm, "end": v(70, 90) * mm});
            skArc(sketch, "E79.7", {"start": v(80, 80) * mm, "mid": v(77.07, 87.07) * mm, "end": v(70, 90) * mm});
            skCircle(sketch, "E79.8", {"center": v(60, 67.5) * mm, "radius": 4 * mm});
            skCircle(sketch, "E79.9", {"center": v(60, -67.5) * mm, "radius": 4 * mm});
            skCircle(sketch, "E79.10", {"center": v(-60, 67.5) * mm, "radius": 4 * mm});
            skCircle(sketch, "E79.11", {"center": v(-60, -67.5) * mm, "radius": 4 * mm});
            skLineSegment(sketch, "E79.12", {"start": v(-60, 40.3) * mm, "end": v(-60, -40.3) * mm});
            skArc(sketch, "E79.13", {"start": v(-56.15, 48.18) * mm, "mid": v(-58.99, 44.68) * mm, "end": v(-60, 40.3) * mm});
            skArc(sketch, "E79.14", {"start": v(56.15, 48.18) * mm, "mid": v(0, 67.5) * mm, "end": v(-56.15, 48.18) * mm});
            skArc(sketch, "E79.15", {"start": v(60, 40.3) * mm, "mid": v(58.99, 44.68) * mm, "end": v(56.15, 48.18) * mm});
            skLineSegment(sketch, "E79.16", {"start": v(60, 40.3) * mm, "end": v(60, -40.3) * mm});
            skArc(sketch, "E79.17", {"start": v(-56.15, -48.18) * mm, "mid": v(0, -67.5) * mm, "end": v(56.15, -48.18) * mm});
            skArc(sketch, "E79.18", {"start": v(56.15, -48.18) * mm, "mid": v(58.99, -44.68) * mm, "end": v(60, -40.3) * mm});
            skArc(sketch, "E79.19", {"start": v(-60, -40.3) * mm, "mid": v(-58.99, -44.68) * mm, "end": v(-56.15, -48.18) * mm});
            skLineSegment(sketch, "E80", {"start": v(-33, 90) * mm, "end": v(-15, 108) * mm});
            skLineSegment(sketch, "E81", {"start": v(-15, 108) * mm, "end": v(-15, 120) * mm});
            skLineSegment(sketch, "E82", {"start": v(33, 90) * mm, "end": v(15, 108) * mm});
            skLineSegment(sketch, "E83", {"start": v(15, 108) * mm, "end": v(15, 120) * mm});
            skArc(sketch, "E84", {"start": v(-15, 120) * mm, "mid": v(0, 135) * mm, "end": v(15, 120) * mm});
            skCircle(sketch, "E85", {"center": v(0, 120) * mm, "radius": 6 * mm});
            skLineSegment(sketch, "E86", {"start": v(0, 90) * mm, "end": v(0, 120) * mm, "construction": true});
            skLineSegment(sketch, "E87", {"start": v(-80, 0) * mm, "end": v(80, 0) * mm, "construction": true});
            skLineSegment(sketch, "E88.MirrorCS", {"start": v(33, -90) * mm, "end": v(15, -108) * mm});
            skLineSegment(sketch, "E89.MirrorCS", {"start": v(-33, -90) * mm, "end": v(-15, -108) * mm});
            skArc(sketch, "E90.MirrorCS", {"start": v(-15, -120) * mm, "mid": v(0, -135) * mm, "end": v(15, -120) * mm});
            skLineSegment(sketch, "E91.MirrorCS", {"start": v(15, -108) * mm, "end": v(15, -120) * mm});
            skLineSegment(sketch, "E92.MirrorCS", {"start": v(-15, -108) * mm, "end": v(-15, -120) * mm});
            skCircle(sketch, "E93.MirrorC", {"center": v(0, -120) * mm, "radius": 6 * mm});
            skLineSegment(sketch, "E94.MirrorCS", {"start": v(0, -90) * mm, "end": v(0, -120) * mm, "construction": true});
            skSolve(sketch);
        }
        {
            var Q0;
            Q0 = qSketchRegion(id + "F16", true);
            var Q1;
            Q1=makeQuery(id+"F2.opExtrude","CAP_FACE",FACE,{"disambiguationData":[OSD([sQuery(id+"F0.wireOp",EDGE,"E12"),sQuery(id+"F0.wireOp",EDGE,"E13"),sQuery(id+"F0.wireOp",EDGE,"E14"),sQuery(id+"F0.wireOp",EDGE,"E15"),sQuery(id+"F0.wireOp",EDGE,"E17.filletArc"),sQuery(id+"F0.wireOp",EDGE,"E18.filletArc"),sQuery(id+"F0.wireOp",EDGE,"E19.filletArc"),sQuery(id+"F0.wireOp",EDGE,"E20.filletArc"),sQuery(id+"F0.wireOp",EDGE,"E25.0"),sQuery(id+"F0.wireOp",EDGE,"E25.1"),sQuery(id+"F0.wireOp",EDGE,"E25.2"),sQuery(id+"F0.wireOp",EDGE,"E25.3"),sQuery(id+"F0.wireOp",EDGE,"E25.4"),sQuery(id+"F0.wireOp",EDGE,"E25.5"),sQuery(id+"F0.wireOp",EDGE,"E25.6"),sQuery(id+"F0.wireOp",EDGE,"E25.7")])],"isStart":false});
            extrude(context, id + "F17", {"entities" : qUnion([Q0]), "endBound" : BoundingType.UP_TO_SURFACE, "endBoundEntityFace" : qUnion([Q1]), "depth" : 25 * mm});
        }
    });
